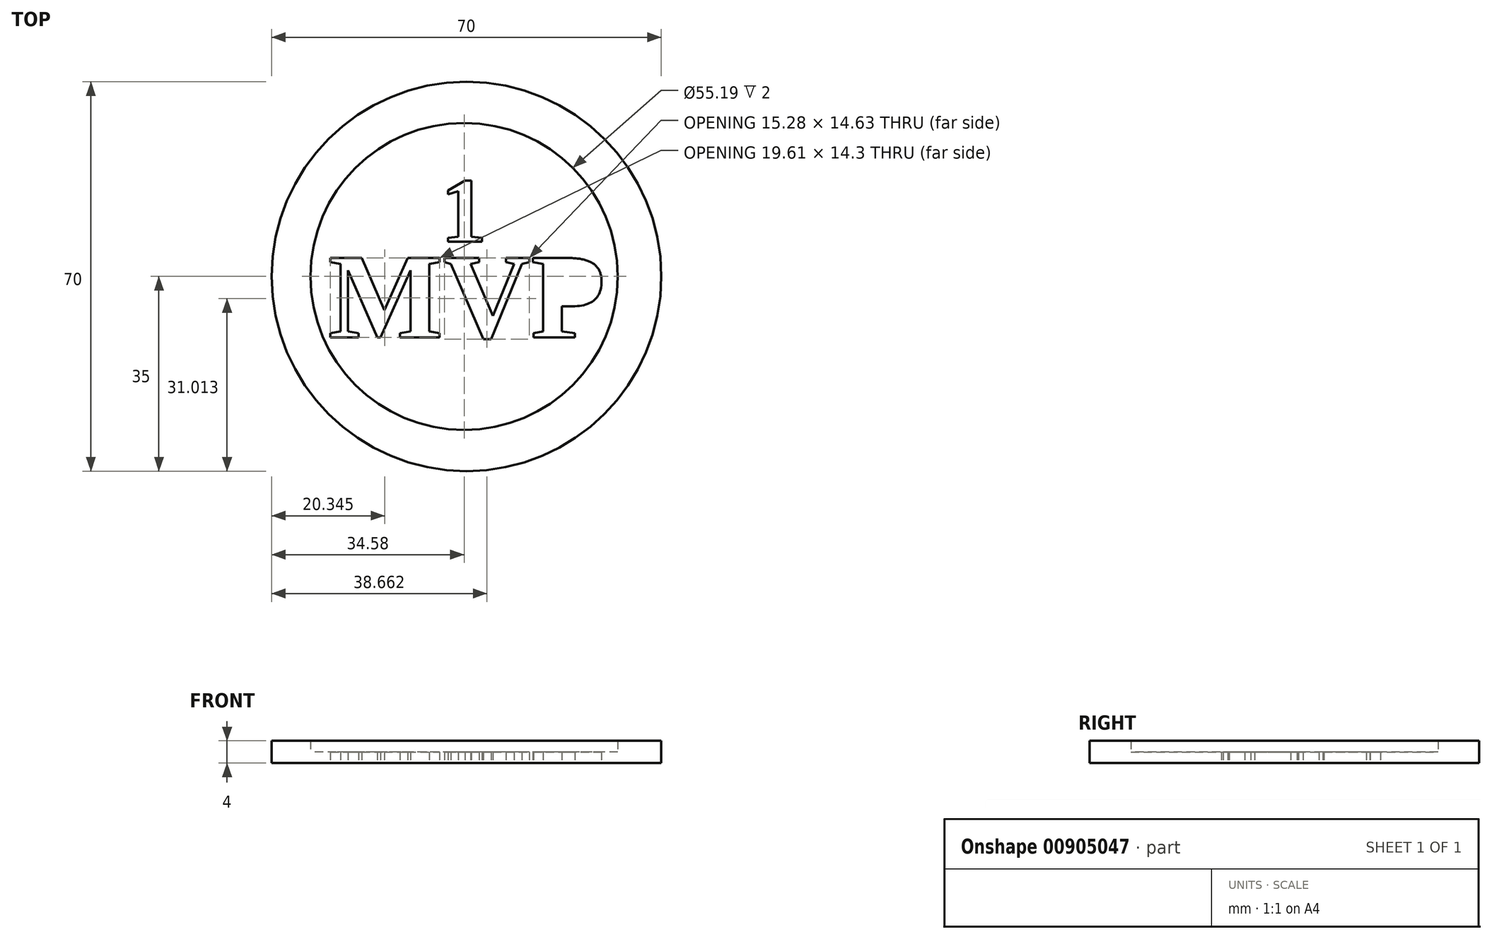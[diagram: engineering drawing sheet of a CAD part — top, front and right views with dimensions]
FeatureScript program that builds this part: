
annotation { "Feature Type Name" : "Feature", "Feature Type Description" : "" }
export const myFeature = defineFeature(function(context is Context, id is Id, definition is map)
    precondition{}
    {
        {
            var Q0;
            Q0=qCreatedBy(makeId("Top.planeOp"),FACE);
            var sketch = newSketch(context, id + "F0", { "sketchPlane" : qUnion([Q0])});
            skCircle(sketch, "E0", {"center": v(0, 0) * mm, "radius": 27.6 * mm});
            skCircle(sketch, "E1", {"center": v(0.42, 0) * mm, "radius": 35 * mm});
            skText(sketch, "E2", { "text": "1 ", "fontName": "Tinos-Bold.ttf"});
            skText(sketch, "E3", { "text": "MVP\n", "fontName": "Tinos-Bold.ttf"});
            const initialGuessF0  = {"E2": [-0.00426, 0.00623, 1, 0, 0.012], "E3": [-0.02441, -0.01097, 1, 0, 0.01572]};
            skSetInitialGuess(sketch, initialGuessF0);
            skSolve(sketch);
        }
        {
            var Q0;
            Q0=makeQuery(id+"F0.imprint","IMPRINT",FACE,{"disambiguationData":[TD([[makeQuery(id+"F0.imprint","IMPRINT",EDGE,{"derivedFrom":sQuery(id+"F0.wireOp",EDGE,"E0")}),1.0]])]});
            extrude(context, id + "F1", {"entities" : qUnion([Q0]), "depth" : 2 * mm, "offsetDistance" : 25.4 * mm});
        }
        {
            var Q0;
            Q0=makeQuery(id+"F0.imprint","IMPRINT",FACE,{"disambiguationData":[TD([[makeQuery(id+"F0.imprint","IMPRINT",EDGE,{"derivedFrom":sQuery(id+"F0.wireOp",EDGE,"E0")}),-1.0]])]});
            extrude(context, id + "F2", {"entities" : qUnion([Q0]), "operationType" : NewBodyOperationType.ADD, "depth" : 4 * mm, "offsetDistance" : 25.4 * mm});
        }
    });
